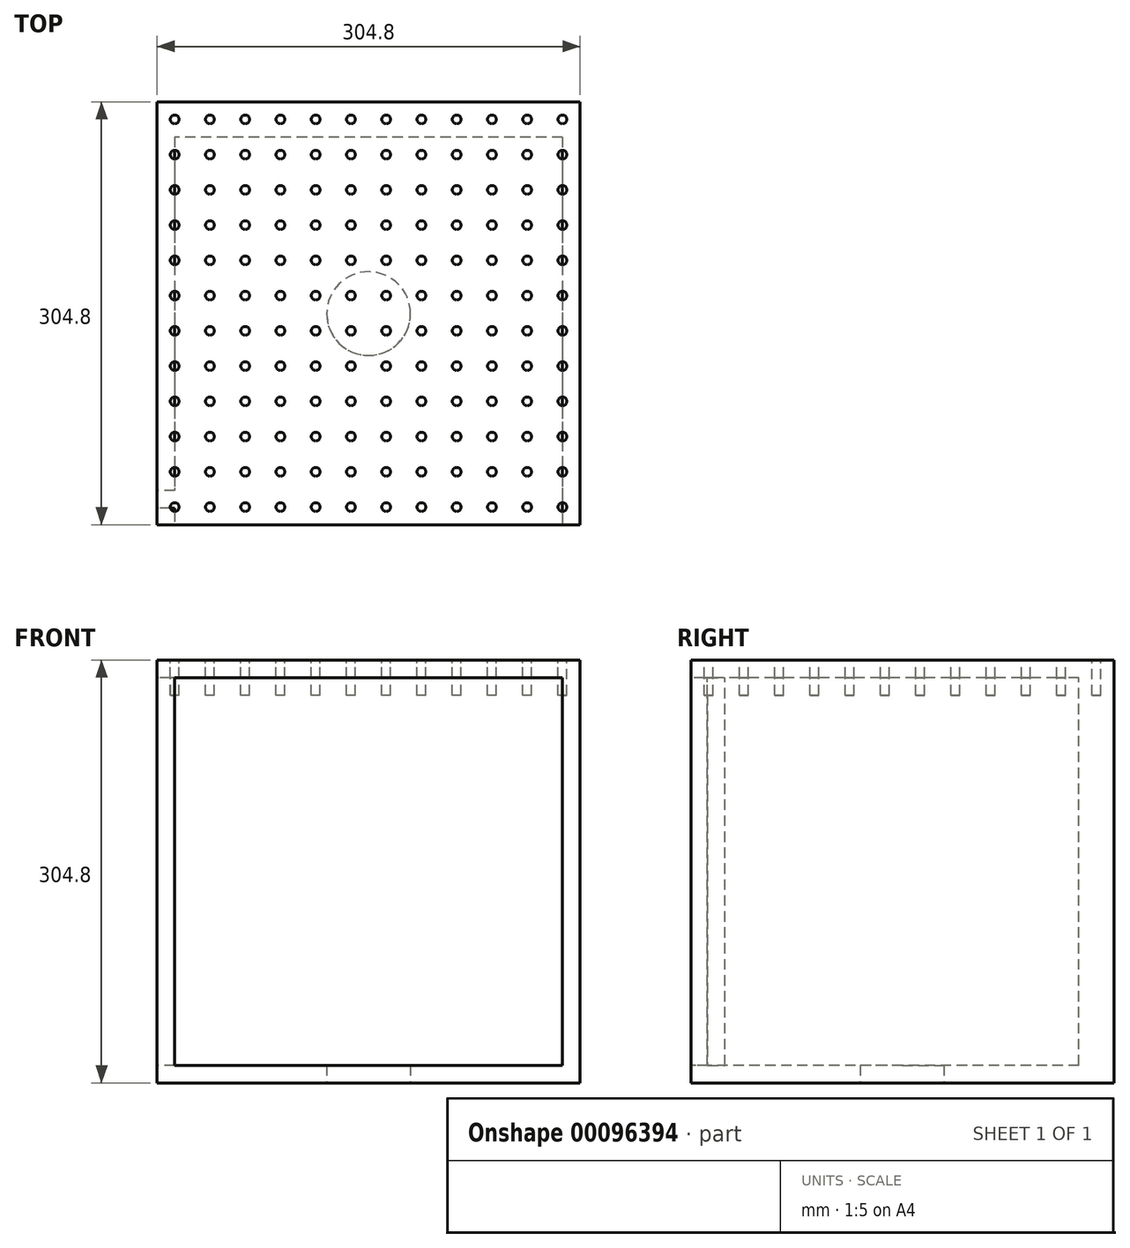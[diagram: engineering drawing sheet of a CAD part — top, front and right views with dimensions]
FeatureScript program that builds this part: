
annotation { "Feature Type Name" : "Feature", "Feature Type Description" : "" }
export const myFeature = defineFeature(function(context is Context, id is Id, definition is map)
    precondition{}
    {
        {
            var Q0;
            Q0=qCreatedBy(makeId("Front.planeOp"),FACE);
            var sketch = newSketch(context, id + "F0", { "sketchPlane" : qUnion([Q0])});
            skLineSegment(sketch, "E0.bottom", {"start": v(152.4, -152.4) * mm, "end": v(-152.4, -152.4) * mm});
            skLineSegment(sketch, "E0.top", {"start": v(152.4, 152.4) * mm, "end": v(-152.4, 152.4) * mm});
            skLineSegment(sketch, "E0.left", {"start": v(152.4, -152.4) * mm, "end": v(152.4, 152.4) * mm});
            skLineSegment(sketch, "E0.right", {"start": v(-152.4, -152.4) * mm, "end": v(-152.4, 152.4) * mm});
            skPoint(sketch, "E0.middle", {"position": v(0, 0) * mm});
            skSolve(sketch);
        }
        {
            var Q0;
            Q0=makeQuery(id+"F0.imprint","IMPRINT",FACE,{"disambiguationData":[TD([[makeQuery(id+"F0.imprint","IMPRINT",EDGE,{"derivedFrom":sQuery(id+"F0.wireOp",EDGE,"E0.bottom")}),-1.0]])]});
            extrude(context, id + "F1", {"entities" : qUnion([Q0]), "oppositeDirection" : true, "depth" : 304.8 * mm});
        }
        {
            var Q0;
            Q0=makeQuery(id+"F1.opExtrude","CAP_FACE",FACE,{"disambiguationData":[OSD([sQuery(id+"F0.wireOp",EDGE,"E0.bottom"),sQuery(id+"F0.wireOp",EDGE,"E0.top"),sQuery(id+"F0.wireOp",EDGE,"E0.left"),sQuery(id+"F0.wireOp",EDGE,"E0.right")])],"isStart":true});
            var sketch = newSketch(context, id + "F2", { "sketchPlane" : qUnion([Q0])});
            skLineSegment(sketch, "E1.bottom", {"start": v(139.7, -139.7) * mm, "end": v(-139.7, -139.7) * mm});
            skLineSegment(sketch, "E1.top", {"start": v(139.7, 139.7) * mm, "end": v(-139.7, 139.7) * mm});
            skLineSegment(sketch, "E1.left", {"start": v(139.7, -139.7) * mm, "end": v(139.7, 139.7) * mm});
            skLineSegment(sketch, "E1.right", {"start": v(-139.7, -139.7) * mm, "end": v(-139.7, 139.7) * mm});
            skPoint(sketch, "E1.middle", {"position": v(0, 0) * mm});
            skSolve(sketch);
        }
        {
            var Q0;
            Q0=makeQuery(id+"F2.imprint","IMPRINT",FACE,{"disambiguationData":[TD([[makeQuery(id+"F2.imprint","IMPRINT",EDGE,{"derivedFrom":sQuery(id+"F2.wireOp",EDGE,"E1.bottom")}),-1.0]])]});
            extrude(context, id + "F3", {"entities" : qUnion([Q0]), "operationType" : NewBodyOperationType.REMOVE, "oppositeDirection" : true, "depth" : 279.4 * mm});
        }
        {
            var Q0;
            Q0=makeQuery(id+"F1.opExtrude","SWEPT_FACE",FACE,{"disambiguationData":[OSD([sQuery(id+"F0.wireOp",EDGE,"E0.right")])]});
            var sketch = newSketch(context, id + "F4", { "sketchPlane" : qUnion([Q0])});
            skLineSegment(sketch, "E2.bottom", {"start": v(-11.8, -139.7) * mm, "end": v(-24.5, -139.7) * mm});
            skLineSegment(sketch, "E2.top", {"start": v(-11.8, 139.7) * mm, "end": v(-24.5, 139.7) * mm});
            skLineSegment(sketch, "E2.left", {"start": v(-11.8, -139.7) * mm, "end": v(-11.8, 139.7) * mm});
            skLineSegment(sketch, "E2.right", {"start": v(-24.5, -139.7) * mm, "end": v(-24.5, 139.7) * mm});
            skPoint(sketch, "E2.middle", {"position": v(-18.15, 0) * mm});
            skSolve(sketch);
        }
        {
            var Q0;
            Q0=makeQuery(id+"F4.imprint","IMPRINT",FACE,{"disambiguationData":[TD([[makeQuery(id+"F4.imprint","IMPRINT",EDGE,{"derivedFrom":sQuery(id+"F4.wireOp",EDGE,"E2.bottom")}),-1.0]])]});
            extrude(context, id + "F5", {"entities" : qUnion([Q0]), "operationType" : NewBodyOperationType.REMOVE, "oppositeDirection" : true, "depth" : 93.46 * mm});
        }
        {
            var Q0;
            Q0=makeQuery(id+"F1.opExtrude","SWEPT_FACE",FACE,{"disambiguationData":[OSD([sQuery(id+"F0.wireOp",EDGE,"E0.top")])]});
            var sketch = newSketch(context, id + "F6", { "sketchPlane" : qUnion([Q0])});
            skLineSegment(sketch, "E3", {"start": v(-152.4, 304.8) * mm, "end": v(-139.7, 304.8) * mm, "construction": true});
            skLineSegment(sketch, "E4", {"start": v(-139.7, 304.8) * mm, "end": v(-139.7, 292.1) * mm, "construction": true});
            skCircle(sketch, "E5", {"center": v(-139.7, 292.1) * mm, "radius": 3.18 * mm});
            skCircle(sketch, "E6.0.1.0", {"center": v(-139.7, 266.7) * mm, "radius": 3.18 * mm});
            skCircle(sketch, "E6.0.2.0", {"center": v(-139.7, 241.3) * mm, "radius": 3.18 * mm});
            skCircle(sketch, "E6.0.3.0", {"center": v(-139.7, 215.9) * mm, "radius": 3.18 * mm});
            skCircle(sketch, "E6.0.4.0", {"center": v(-139.7, 190.5) * mm, "radius": 3.18 * mm});
            skCircle(sketch, "E6.0.5.0", {"center": v(-139.7, 165.1) * mm, "radius": 3.18 * mm});
            skCircle(sketch, "E6.0.6.0", {"center": v(-139.7, 139.7) * mm, "radius": 3.18 * mm});
            skCircle(sketch, "E6.0.7.0", {"center": v(-139.7, 114.3) * mm, "radius": 3.18 * mm});
            skCircle(sketch, "E6.0.8.0", {"center": v(-139.7, 88.9) * mm, "radius": 3.18 * mm});
            skCircle(sketch, "E6.0.9.0", {"center": v(-139.7, 63.5) * mm, "radius": 3.18 * mm});
            skCircle(sketch, "E6.0.10.0", {"center": v(-139.7, 38.1) * mm, "radius": 3.18 * mm});
            skCircle(sketch, "E6.0.11.0", {"center": v(-139.7, 12.7) * mm, "radius": 3.18 * mm});
            skCircle(sketch, "E6.1.0.0", {"center": v(-114.3, 292.1) * mm, "radius": 3.18 * mm});
            skCircle(sketch, "E6.1.1.0", {"center": v(-114.3, 266.7) * mm, "radius": 3.18 * mm});
            skCircle(sketch, "E6.1.2.0", {"center": v(-114.3, 241.3) * mm, "radius": 3.18 * mm});
            skCircle(sketch, "E6.1.3.0", {"center": v(-114.3, 215.9) * mm, "radius": 3.18 * mm});
            skCircle(sketch, "E6.1.4.0", {"center": v(-114.3, 190.5) * mm, "radius": 3.18 * mm});
            skCircle(sketch, "E6.1.5.0", {"center": v(-114.3, 165.1) * mm, "radius": 3.18 * mm});
            skCircle(sketch, "E6.1.6.0", {"center": v(-114.3, 139.7) * mm, "radius": 3.18 * mm});
            skCircle(sketch, "E6.1.7.0", {"center": v(-114.3, 114.3) * mm, "radius": 3.18 * mm});
            skCircle(sketch, "E6.1.8.0", {"center": v(-114.3, 88.9) * mm, "radius": 3.18 * mm});
            skCircle(sketch, "E6.1.9.0", {"center": v(-114.3, 63.5) * mm, "radius": 3.18 * mm});
            skCircle(sketch, "E6.1.10.0", {"center": v(-114.3, 38.1) * mm, "radius": 3.18 * mm});
            skCircle(sketch, "E6.1.11.0", {"center": v(-114.3, 12.7) * mm, "radius": 3.18 * mm});
            skCircle(sketch, "E6.2.0.0", {"center": v(-88.9, 292.1) * mm, "radius": 3.18 * mm});
            skCircle(sketch, "E6.2.1.0", {"center": v(-88.9, 266.7) * mm, "radius": 3.18 * mm});
            skCircle(sketch, "E6.2.2.0", {"center": v(-88.9, 241.3) * mm, "radius": 3.18 * mm});
            skCircle(sketch, "E6.2.3.0", {"center": v(-88.9, 215.9) * mm, "radius": 3.18 * mm});
            skCircle(sketch, "E6.2.4.0", {"center": v(-88.9, 190.5) * mm, "radius": 3.18 * mm});
            skCircle(sketch, "E6.2.5.0", {"center": v(-88.9, 165.1) * mm, "radius": 3.18 * mm});
            skCircle(sketch, "E6.2.6.0", {"center": v(-88.9, 139.7) * mm, "radius": 3.18 * mm});
            skCircle(sketch, "E6.2.7.0", {"center": v(-88.9, 114.3) * mm, "radius": 3.18 * mm});
            skCircle(sketch, "E6.2.8.0", {"center": v(-88.9, 88.9) * mm, "radius": 3.18 * mm});
            skCircle(sketch, "E6.2.9.0", {"center": v(-88.9, 63.5) * mm, "radius": 3.18 * mm});
            skCircle(sketch, "E6.2.10.0", {"center": v(-88.9, 38.1) * mm, "radius": 3.18 * mm});
            skCircle(sketch, "E6.2.11.0", {"center": v(-88.9, 12.7) * mm, "radius": 3.18 * mm});
            skCircle(sketch, "E6.3.0.0", {"center": v(-63.5, 292.1) * mm, "radius": 3.18 * mm});
            skCircle(sketch, "E6.3.1.0", {"center": v(-63.5, 266.7) * mm, "radius": 3.18 * mm});
            skCircle(sketch, "E6.3.2.0", {"center": v(-63.5, 241.3) * mm, "radius": 3.18 * mm});
            skCircle(sketch, "E6.3.3.0", {"center": v(-63.5, 215.9) * mm, "radius": 3.18 * mm});
            skCircle(sketch, "E6.3.4.0", {"center": v(-63.5, 190.5) * mm, "radius": 3.18 * mm});
            skCircle(sketch, "E6.3.5.0", {"center": v(-63.5, 165.1) * mm, "radius": 3.18 * mm});
            skCircle(sketch, "E6.3.6.0", {"center": v(-63.5, 139.7) * mm, "radius": 3.18 * mm});
            skCircle(sketch, "E6.3.7.0", {"center": v(-63.5, 114.3) * mm, "radius": 3.18 * mm});
            skCircle(sketch, "E6.3.8.0", {"center": v(-63.5, 88.9) * mm, "radius": 3.18 * mm});
            skCircle(sketch, "E6.3.9.0", {"center": v(-63.5, 63.5) * mm, "radius": 3.18 * mm});
            skCircle(sketch, "E6.3.10.0", {"center": v(-63.5, 38.1) * mm, "radius": 3.18 * mm});
            skCircle(sketch, "E6.3.11.0", {"center": v(-63.5, 12.7) * mm, "radius": 3.18 * mm});
            skCircle(sketch, "E6.4.0.0", {"center": v(-38.1, 292.1) * mm, "radius": 3.18 * mm});
            skCircle(sketch, "E6.4.1.0", {"center": v(-38.1, 266.7) * mm, "radius": 3.18 * mm});
            skCircle(sketch, "E6.4.2.0", {"center": v(-38.1, 241.3) * mm, "radius": 3.18 * mm});
            skCircle(sketch, "E6.4.3.0", {"center": v(-38.1, 215.9) * mm, "radius": 3.18 * mm});
            skCircle(sketch, "E6.4.4.0", {"center": v(-38.1, 190.5) * mm, "radius": 3.18 * mm});
            skCircle(sketch, "E6.4.5.0", {"center": v(-38.1, 165.1) * mm, "radius": 3.18 * mm});
            skCircle(sketch, "E6.4.6.0", {"center": v(-38.1, 139.7) * mm, "radius": 3.18 * mm});
            skCircle(sketch, "E6.4.7.0", {"center": v(-38.1, 114.3) * mm, "radius": 3.18 * mm});
            skCircle(sketch, "E6.4.8.0", {"center": v(-38.1, 88.9) * mm, "radius": 3.18 * mm});
            skCircle(sketch, "E6.4.9.0", {"center": v(-38.1, 63.5) * mm, "radius": 3.18 * mm});
            skCircle(sketch, "E6.4.10.0", {"center": v(-38.1, 38.1) * mm, "radius": 3.18 * mm});
            skCircle(sketch, "E6.4.11.0", {"center": v(-38.1, 12.7) * mm, "radius": 3.18 * mm});
            skCircle(sketch, "E6.5.0.0", {"center": v(-12.7, 292.1) * mm, "radius": 3.18 * mm});
            skCircle(sketch, "E6.5.1.0", {"center": v(-12.7, 266.7) * mm, "radius": 3.18 * mm});
            skCircle(sketch, "E6.5.2.0", {"center": v(-12.7, 241.3) * mm, "radius": 3.18 * mm});
            skCircle(sketch, "E6.5.3.0", {"center": v(-12.7, 215.9) * mm, "radius": 3.18 * mm});
            skCircle(sketch, "E6.5.4.0", {"center": v(-12.7, 190.5) * mm, "radius": 3.18 * mm});
            skCircle(sketch, "E6.5.5.0", {"center": v(-12.7, 165.1) * mm, "radius": 3.18 * mm});
            skCircle(sketch, "E6.5.6.0", {"center": v(-12.7, 139.7) * mm, "radius": 3.18 * mm});
            skCircle(sketch, "E6.5.7.0", {"center": v(-12.7, 114.3) * mm, "radius": 3.18 * mm});
            skCircle(sketch, "E6.5.8.0", {"center": v(-12.7, 88.9) * mm, "radius": 3.18 * mm});
            skCircle(sketch, "E6.5.9.0", {"center": v(-12.7, 63.5) * mm, "radius": 3.18 * mm});
            skCircle(sketch, "E6.5.10.0", {"center": v(-12.7, 38.1) * mm, "radius": 3.18 * mm});
            skCircle(sketch, "E6.5.11.0", {"center": v(-12.7, 12.7) * mm, "radius": 3.18 * mm});
            skCircle(sketch, "E6.6.0.0", {"center": v(12.7, 292.1) * mm, "radius": 3.18 * mm});
            skCircle(sketch, "E6.6.1.0", {"center": v(12.7, 266.7) * mm, "radius": 3.18 * mm});
            skCircle(sketch, "E6.6.2.0", {"center": v(12.7, 241.3) * mm, "radius": 3.18 * mm});
            skCircle(sketch, "E6.6.3.0", {"center": v(12.7, 215.9) * mm, "radius": 3.18 * mm});
            skCircle(sketch, "E6.6.4.0", {"center": v(12.7, 190.5) * mm, "radius": 3.18 * mm});
            skCircle(sketch, "E6.6.5.0", {"center": v(12.7, 165.1) * mm, "radius": 3.18 * mm});
            skCircle(sketch, "E6.6.6.0", {"center": v(12.7, 139.7) * mm, "radius": 3.18 * mm});
            skCircle(sketch, "E6.6.7.0", {"center": v(12.7, 114.3) * mm, "radius": 3.18 * mm});
            skCircle(sketch, "E6.6.8.0", {"center": v(12.7, 88.9) * mm, "radius": 3.18 * mm});
            skCircle(sketch, "E6.6.9.0", {"center": v(12.7, 63.5) * mm, "radius": 3.18 * mm});
            skCircle(sketch, "E6.6.10.0", {"center": v(12.7, 38.1) * mm, "radius": 3.18 * mm});
            skCircle(sketch, "E6.6.11.0", {"center": v(12.7, 12.7) * mm, "radius": 3.18 * mm});
            skCircle(sketch, "E6.7.0.0", {"center": v(38.1, 292.1) * mm, "radius": 3.18 * mm});
            skCircle(sketch, "E6.7.1.0", {"center": v(38.1, 266.7) * mm, "radius": 3.18 * mm});
            skCircle(sketch, "E6.7.2.0", {"center": v(38.1, 241.3) * mm, "radius": 3.18 * mm});
            skCircle(sketch, "E6.7.3.0", {"center": v(38.1, 215.9) * mm, "radius": 3.18 * mm});
            skCircle(sketch, "E6.7.4.0", {"center": v(38.1, 190.5) * mm, "radius": 3.18 * mm});
            skCircle(sketch, "E6.7.5.0", {"center": v(38.1, 165.1) * mm, "radius": 3.18 * mm});
            skCircle(sketch, "E6.7.6.0", {"center": v(38.1, 139.7) * mm, "radius": 3.18 * mm});
            skCircle(sketch, "E6.7.7.0", {"center": v(38.1, 114.3) * mm, "radius": 3.18 * mm});
            skCircle(sketch, "E6.7.8.0", {"center": v(38.1, 88.9) * mm, "radius": 3.18 * mm});
            skCircle(sketch, "E6.7.9.0", {"center": v(38.1, 63.5) * mm, "radius": 3.18 * mm});
            skCircle(sketch, "E6.7.10.0", {"center": v(38.1, 38.1) * mm, "radius": 3.18 * mm});
            skCircle(sketch, "E6.7.11.0", {"center": v(38.1, 12.7) * mm, "radius": 3.18 * mm});
            skCircle(sketch, "E6.8.0.0", {"center": v(63.5, 292.1) * mm, "radius": 3.18 * mm});
            skCircle(sketch, "E6.8.1.0", {"center": v(63.5, 266.7) * mm, "radius": 3.18 * mm});
            skCircle(sketch, "E6.8.2.0", {"center": v(63.5, 241.3) * mm, "radius": 3.18 * mm});
            skCircle(sketch, "E6.8.3.0", {"center": v(63.5, 215.9) * mm, "radius": 3.18 * mm});
            skCircle(sketch, "E6.8.4.0", {"center": v(63.5, 190.5) * mm, "radius": 3.18 * mm});
            skCircle(sketch, "E6.8.5.0", {"center": v(63.5, 165.1) * mm, "radius": 3.18 * mm});
            skCircle(sketch, "E6.8.6.0", {"center": v(63.5, 139.7) * mm, "radius": 3.18 * mm});
            skCircle(sketch, "E6.8.7.0", {"center": v(63.5, 114.3) * mm, "radius": 3.18 * mm});
            skCircle(sketch, "E6.8.8.0", {"center": v(63.5, 88.9) * mm, "radius": 3.18 * mm});
            skCircle(sketch, "E6.8.9.0", {"center": v(63.5, 63.5) * mm, "radius": 3.18 * mm});
            skCircle(sketch, "E6.8.10.0", {"center": v(63.5, 38.1) * mm, "radius": 3.18 * mm});
            skCircle(sketch, "E6.8.11.0", {"center": v(63.5, 12.7) * mm, "radius": 3.18 * mm});
            skCircle(sketch, "E6.9.0.0", {"center": v(88.9, 292.1) * mm, "radius": 3.18 * mm});
            skCircle(sketch, "E6.9.1.0", {"center": v(88.9, 266.7) * mm, "radius": 3.18 * mm});
            skCircle(sketch, "E6.9.2.0", {"center": v(88.9, 241.3) * mm, "radius": 3.18 * mm});
            skCircle(sketch, "E6.9.3.0", {"center": v(88.9, 215.9) * mm, "radius": 3.18 * mm});
            skCircle(sketch, "E6.9.4.0", {"center": v(88.9, 190.5) * mm, "radius": 3.18 * mm});
            skCircle(sketch, "E6.9.5.0", {"center": v(88.9, 165.1) * mm, "radius": 3.18 * mm});
            skCircle(sketch, "E6.9.6.0", {"center": v(88.9, 139.7) * mm, "radius": 3.18 * mm});
            skCircle(sketch, "E6.9.7.0", {"center": v(88.9, 114.3) * mm, "radius": 3.18 * mm});
            skCircle(sketch, "E6.9.8.0", {"center": v(88.9, 88.9) * mm, "radius": 3.18 * mm});
            skCircle(sketch, "E6.9.9.0", {"center": v(88.9, 63.5) * mm, "radius": 3.18 * mm});
            skCircle(sketch, "E6.9.10.0", {"center": v(88.9, 38.1) * mm, "radius": 3.18 * mm});
            skCircle(sketch, "E6.9.11.0", {"center": v(88.9, 12.7) * mm, "radius": 3.18 * mm});
            skCircle(sketch, "E6.10.0.0", {"center": v(114.3, 292.1) * mm, "radius": 3.18 * mm});
            skCircle(sketch, "E6.10.1.0", {"center": v(114.3, 266.7) * mm, "radius": 3.18 * mm});
            skCircle(sketch, "E6.10.2.0", {"center": v(114.3, 241.3) * mm, "radius": 3.18 * mm});
            skCircle(sketch, "E6.10.3.0", {"center": v(114.3, 215.9) * mm, "radius": 3.18 * mm});
            skCircle(sketch, "E6.10.4.0", {"center": v(114.3, 190.5) * mm, "radius": 3.18 * mm});
            skCircle(sketch, "E6.10.5.0", {"center": v(114.3, 165.1) * mm, "radius": 3.18 * mm});
            skCircle(sketch, "E6.10.6.0", {"center": v(114.3, 139.7) * mm, "radius": 3.18 * mm});
            skCircle(sketch, "E6.10.7.0", {"center": v(114.3, 114.3) * mm, "radius": 3.18 * mm});
            skCircle(sketch, "E6.10.8.0", {"center": v(114.3, 88.9) * mm, "radius": 3.18 * mm});
            skCircle(sketch, "E6.10.9.0", {"center": v(114.3, 63.5) * mm, "radius": 3.18 * mm});
            skCircle(sketch, "E6.10.10.0", {"center": v(114.3, 38.1) * mm, "radius": 3.18 * mm});
            skCircle(sketch, "E6.10.11.0", {"center": v(114.3, 12.7) * mm, "radius": 3.18 * mm});
            skCircle(sketch, "E6.11.0.0", {"center": v(139.7, 292.1) * mm, "radius": 3.18 * mm});
            skCircle(sketch, "E6.11.1.0", {"center": v(139.7, 266.7) * mm, "radius": 3.18 * mm});
            skCircle(sketch, "E6.11.2.0", {"center": v(139.7, 241.3) * mm, "radius": 3.18 * mm});
            skCircle(sketch, "E6.11.3.0", {"center": v(139.7, 215.9) * mm, "radius": 3.18 * mm});
            skCircle(sketch, "E6.11.4.0", {"center": v(139.7, 190.5) * mm, "radius": 3.18 * mm});
            skCircle(sketch, "E6.11.5.0", {"center": v(139.7, 165.1) * mm, "radius": 3.18 * mm});
            skCircle(sketch, "E6.11.6.0", {"center": v(139.7, 139.7) * mm, "radius": 3.18 * mm});
            skCircle(sketch, "E6.11.7.0", {"center": v(139.7, 114.3) * mm, "radius": 3.18 * mm});
            skCircle(sketch, "E6.11.8.0", {"center": v(139.7, 88.9) * mm, "radius": 3.18 * mm});
            skCircle(sketch, "E6.11.9.0", {"center": v(139.7, 63.5) * mm, "radius": 3.18 * mm});
            skCircle(sketch, "E6.11.10.0", {"center": v(139.7, 38.1) * mm, "radius": 3.18 * mm});
            skCircle(sketch, "E6.11.11.0", {"center": v(139.7, 12.7) * mm, "radius": 3.18 * mm});
            skLineSegment(sketch, "E6.direction1", {"start": v(-139.7, 292.1) * mm, "end": v(-114.3, 292.1) * mm, "construction": true});
            skLineSegment(sketch, "E6.direction2", {"start": v(-139.7, 292.1) * mm, "end": v(-139.7, 266.7) * mm, "construction": true});
            skSolve(sketch);
        }
        {
            var Q0;
            Q0 = qSketchRegion(id + "F6", true);
            extrude(context, id + "F7", {"entities" : qUnion([Q0]), "operationType" : NewBodyOperationType.REMOVE, "oppositeDirection" : true, "depth" : 25.4 * mm});
        }
        {
            var Q0;
            Q0=makeQuery(id+"F1.opExtrude","SWEPT_FACE",FACE,{"disambiguationData":[OSD([sQuery(id+"F0.wireOp",EDGE,"E0.bottom")])]});
            var sketch = newSketch(context, id + "F8", { "sketchPlane" : qUnion([Q0])});
            skCircle(sketch, "E7", {"center": v(0, -152.12) * mm, "radius": 30.16 * mm});
            skSolve(sketch);
        }
        {
            var Q0;
            Q0 = qSketchRegion(id + "F8", true);
            extrude(context, id + "F9", {"entities" : qUnion([Q0]), "operationType" : NewBodyOperationType.REMOVE, "oppositeDirection" : true, "depth" : 25.4 * mm});
        }
    });
